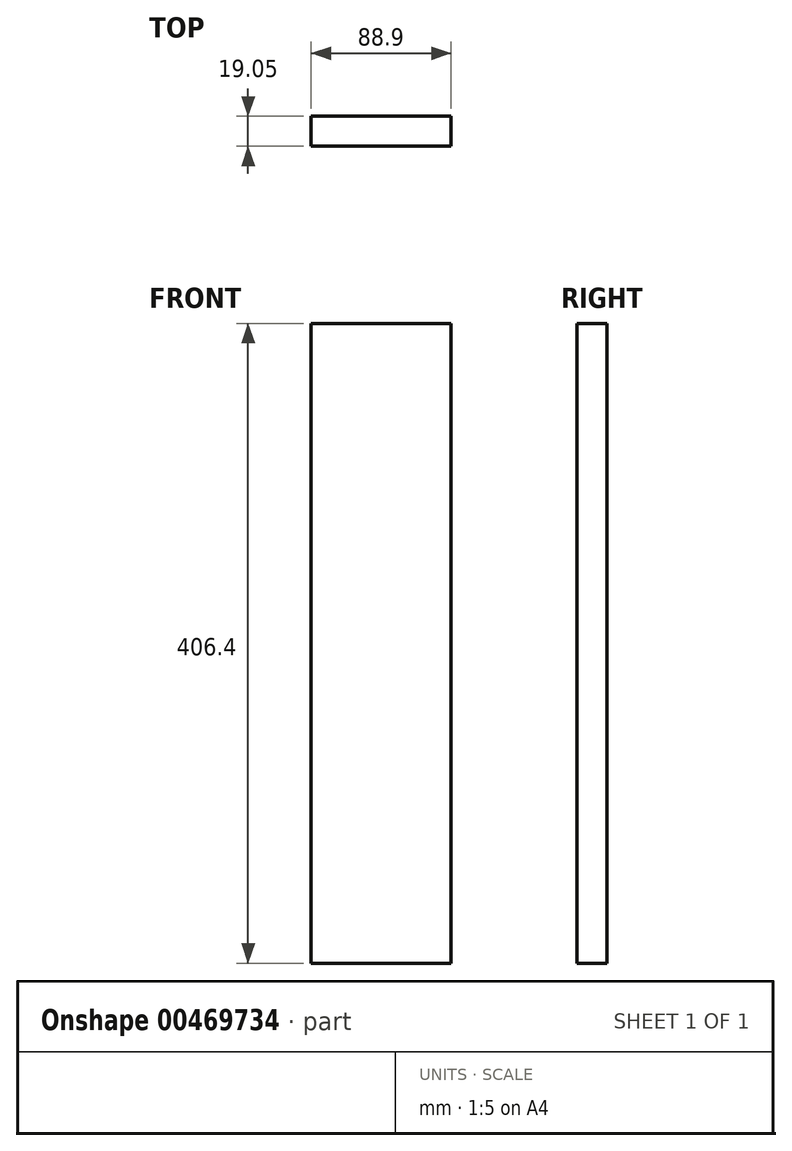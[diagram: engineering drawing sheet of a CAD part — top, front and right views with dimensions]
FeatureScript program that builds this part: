
annotation { "Feature Type Name" : "Feature", "Feature Type Description" : "" }
export const myFeature = defineFeature(function(context is Context, id is Id, definition is map)
    precondition{}
    {
        {
            var Q0;
            Q0=qCreatedBy(makeId("Front.planeOp"),FACE);
            var sketch = newSketch(context, id + "F0", { "sketchPlane" : qUnion([Q0])});
            skLineSegment(sketch, "E0.bottom", {"start": v(0, 0) * mm, "end": v(88.9, 0) * mm});
            skLineSegment(sketch, "E0.top", {"start": v(0, 406.4) * mm, "end": v(88.9, 406.4) * mm});
            skLineSegment(sketch, "E0.left", {"start": v(0, 0) * mm, "end": v(0, 406.4) * mm});
            skLineSegment(sketch, "E0.right", {"start": v(88.9, 0) * mm, "end": v(88.9, 406.4) * mm});
            skSolve(sketch);
        }
        {
            var Q0;
            Q0=makeQuery(id+"F0.imprint","IMPRINT",FACE,{"disambiguationData":[TD([[makeQuery(id+"F0.imprint","IMPRINT",EDGE,{"derivedFrom":sQuery(id+"F0.wireOp",EDGE,"E0.bottom")}),1.0]])]});
            extrude(context, id + "F1", {"entities" : qUnion([Q0]), "depth" : 19.05 * mm, "offsetDistance" : 25.4 * mm});
        }
    });
